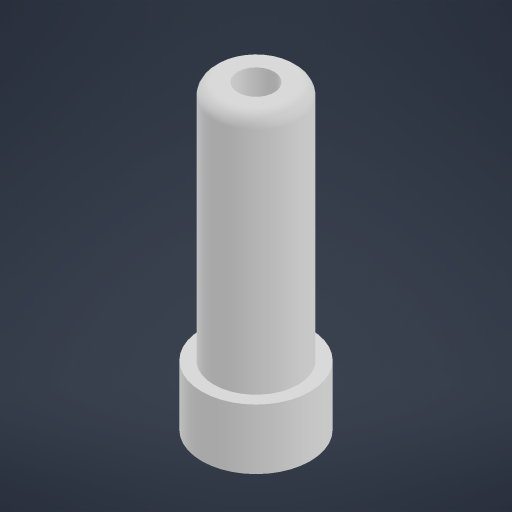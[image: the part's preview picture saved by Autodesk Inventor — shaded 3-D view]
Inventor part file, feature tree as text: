
AUTODESK INVENTOR PART (.ipt)
format: ipt  version: 2024.1 (Build 281209000, 209)  size: 179,712 bytes
history: native  units: mm
features: extrude x2, sketch x1, fillet x1
ambient origin geometry x8: Origin, YZ Plane, XZ Plane, XY Plane, X Axis, Y Axis, Z Axis, Center Point
bodies: Body1 (feature_tree)
feature tree (4):
  sketch  "Sketch5"  dims[d43=9.0mm d44=4.5mm d45=3.0mm d46=7.0mm d47=5.0mm d48=0.0mm d49=20.0mm d50=0.0mm d51=1.0mm]
  extrude  "Extrusion9"  Depth=4.5mm
  extrude  "Extrusion10"  Depth=1.0mm
  fillet  "Fillet3"  Radius=7.0mm
